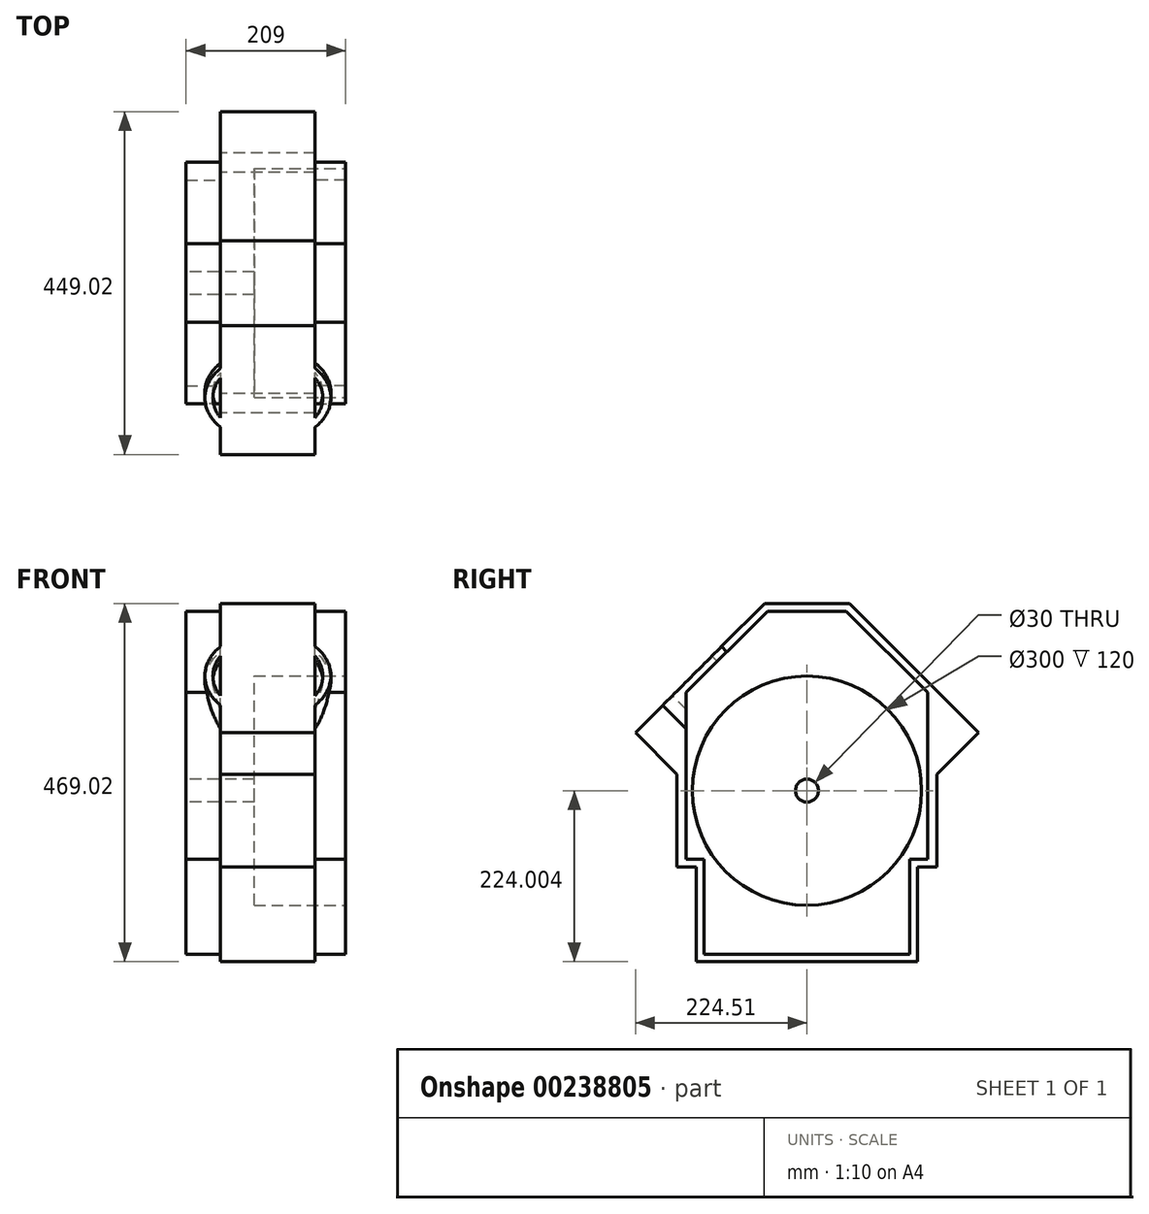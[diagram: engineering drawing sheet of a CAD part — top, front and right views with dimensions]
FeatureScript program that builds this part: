
annotation { "Feature Type Name" : "Feature", "Feature Type Description" : "" }
export const myFeature = defineFeature(function(context is Context, id is Id, definition is map)
    precondition{}
    {
        {
            var Q0;
            Q0=qCreatedBy(makeId("Right.planeOp"),FACE);
            var sketch = newSketch(context, id + "F0", { "sketchPlane" : qUnion([Q0])});
            skLineSegment(sketch, "E0", {"start": v(-150.26, 139.75) * mm, "end": v(-224.5, 65.5) * mm});
            skLineSegment(sketch, "E1", {"start": v(-150.26, 139.75) * mm, "end": v(-55.5, 234.5) * mm});
            skLineSegment(sketch, "E2", {"start": v(-55.5, 234.5) * mm, "end": v(55.5, 234.5) * mm});
            skLineSegment(sketch, "E3", {"start": v(150.26, 139.75) * mm, "end": v(55.5, 234.5) * mm});
            skLineSegment(sketch, "E4", {"start": v(150.26, 139.75) * mm, "end": v(224.5, 65.5) * mm});
            skLineSegment(sketch, "E5", {"start": v(170, 11) * mm, "end": v(224.5, 65.5) * mm});
            skLineSegment(sketch, "E6", {"start": v(170, 11) * mm, "end": v(170, -110.5) * mm});
            skLineSegment(sketch, "E7", {"start": v(144.78, -110.5) * mm, "end": v(170, -110.5) * mm});
            skLineSegment(sketch, "E8", {"start": v(144.78, -110.5) * mm, "end": v(144.78, -234.5) * mm});
            skLineSegment(sketch, "E9", {"start": v(-144.78, -234.5) * mm, "end": v(144.78, -234.5) * mm});
            skLineSegment(sketch, "E10", {"start": v(-144.78, -110.5) * mm, "end": v(-144.78, -234.5) * mm});
            skLineSegment(sketch, "E11", {"start": v(-144.78, -110.5) * mm, "end": v(-170, -110.5) * mm});
            skLineSegment(sketch, "E12", {"start": v(-170, 11) * mm, "end": v(-170, -110.5) * mm});
            skLineSegment(sketch, "E13", {"start": v(-170, 11) * mm, "end": v(-224.5, 65.5) * mm});
            skCircle(sketch, "E14", {"center": v(0, -10.5) * mm, "radius": 15 * mm});
            skSolve(sketch);
        }
        {
            var Q0;
            Q0=makeQuery(id+"F0.imprint","IMPRINT",FACE,{"disambiguationData":[TD([[makeQuery(id+"F0.imprint","IMPRINT",EDGE,{"derivedFrom":sQuery(id+"F0.wireOp",EDGE,"E0")}),1.0]])]});
            extrude(context, id + "F1", {"entities" : qUnion([Q0]), "depth" : 124 * mm});
        }
        {
            var Q0;
            Q0=makeQuery(id+"F1.opExtrude","CAP_FACE",FACE,{"disambiguationData":[OSD([sQuery(id+"F0.wireOp",EDGE,"E0"),sQuery(id+"F0.wireOp",EDGE,"E1"),sQuery(id+"F0.wireOp",EDGE,"E2"),sQuery(id+"F0.wireOp",EDGE,"E3"),sQuery(id+"F0.wireOp",EDGE,"E4"),sQuery(id+"F0.wireOp",EDGE,"E5"),sQuery(id+"F0.wireOp",EDGE,"E6"),sQuery(id+"F0.wireOp",EDGE,"E7"),sQuery(id+"F0.wireOp",EDGE,"E8"),sQuery(id+"F0.wireOp",EDGE,"E9"),sQuery(id+"F0.wireOp",EDGE,"E10"),sQuery(id+"F0.wireOp",EDGE,"E11"),sQuery(id+"F0.wireOp",EDGE,"E12"),sQuery(id+"F0.wireOp",EDGE,"E13"),sQuery(id+"F0.wireOp",EDGE,"E14")])],"isStart":false});
            var sketch = newSketch(context, id + "F2", { "sketchPlane" : qUnion([Q0])});
            skLineSegment(sketch, "E15.bottom", {"start": v(-51.37, 224.5) * mm, "end": v(0, 224.5) * mm});
            skPoint(sketch, "E16", {"position": v(0, -10.5) * mm});
            skLineSegment(sketch, "E17.0", {"start": v(-224.5, 65.5) * mm, "end": v(-55.5, 234.5) * mm});
            skLineSegment(sketch, "E18.0", {"start": v(-158, 117.87) * mm, "end": v(-51.37, 224.5) * mm});
            skLineSegment(sketch, "E19", {"start": v(0, -10.5) * mm, "end": v(0, 224.5) * mm});
            skPoint(sketch, "E20.MirrorCS.start.orphan", {"position": v(90, 185.87) * mm});
            skLineSegment(sketch, "E21", {"start": v(-158, -100.5) * mm, "end": v(-158, 117.87) * mm});
            skPoint(sketch, "E22.orphan", {"position": v(-90, 185.87) * mm});
            skLineSegment(sketch, "E23", {"start": v(-158, -100.5) * mm, "end": v(-134.78, -100.5) * mm});
            skLineSegment(sketch, "E24", {"start": v(-134.78, -100.5) * mm, "end": v(-134.78, -224.5) * mm});
            skLineSegment(sketch, "E25", {"start": v(-134.78, -224.5) * mm, "end": v(0, -224.5) * mm});
            skPoint(sketch, "E26.orphan", {"position": v(51.37, 224.5) * mm});
            skLineSegment(sketch, "E27.MirrorCS", {"start": v(51.37, 224.5) * mm, "end": v(0, 224.5) * mm});
            skLineSegment(sketch, "E28.MirrorCS", {"start": v(158, 117.87) * mm, "end": v(51.37, 224.5) * mm});
            skLineSegment(sketch, "E29.MirrorCS", {"start": v(158, -100.5) * mm, "end": v(158, 117.87) * mm});
            skLineSegment(sketch, "E30.MirrorCS", {"start": v(158, -100.5) * mm, "end": v(134.78, -100.5) * mm});
            skLineSegment(sketch, "E31.MirrorCS", {"start": v(134.78, -100.5) * mm, "end": v(134.78, -224.5) * mm});
            skLineSegment(sketch, "E32.MirrorCS", {"start": v(134.78, -224.5) * mm, "end": v(0, -224.5) * mm});
            skSolve(sketch);
        }
        {
            var Q0;
            Q0=makeQuery(id+"F2.imprint","IMPRINT",FACE,{"disambiguationData":[TD([[makeQuery(id+"F2.imprint","IMPRINT",EDGE,{"derivedFrom":sQuery(id+"F2.wireOp",EDGE,"E15.bottom")}),-1.0]])]});
            extrude(context, id + "F3", {"entities" : qUnion([Q0]), "operationType" : NewBodyOperationType.ADD, "depth" : 40 * mm});
        }
        {
            var Q0;
            Q0=makeQuery(id+"F1.opExtrude","CAP_FACE",FACE,{"disambiguationData":[OSD([sQuery(id+"F0.wireOp",EDGE,"E0"),sQuery(id+"F0.wireOp",EDGE,"E1"),sQuery(id+"F0.wireOp",EDGE,"E2"),sQuery(id+"F0.wireOp",EDGE,"E3"),sQuery(id+"F0.wireOp",EDGE,"E4"),sQuery(id+"F0.wireOp",EDGE,"E5"),sQuery(id+"F0.wireOp",EDGE,"E6"),sQuery(id+"F0.wireOp",EDGE,"E7"),sQuery(id+"F0.wireOp",EDGE,"E8"),sQuery(id+"F0.wireOp",EDGE,"E9"),sQuery(id+"F0.wireOp",EDGE,"E10"),sQuery(id+"F0.wireOp",EDGE,"E11"),sQuery(id+"F0.wireOp",EDGE,"E12"),sQuery(id+"F0.wireOp",EDGE,"E13"),sQuery(id+"F0.wireOp",EDGE,"E14")])],"isStart":true});
            var sketch = newSketch(context, id + "F4", { "sketchPlane" : qUnion([Q0])});
            skLineSegment(sketch, "E33.0", {"start": v(158, -100.5) * mm, "end": v(158, 117.87) * mm});
            skLineSegment(sketch, "E33.1", {"start": v(158, 117.87) * mm, "end": v(51.37, 224.5) * mm});
            skLineSegment(sketch, "E33.2", {"start": v(51.37, 224.5) * mm, "end": v(0, 224.5) * mm});
            skLineSegment(sketch, "E33.3", {"start": v(-51.37, 224.5) * mm, "end": v(0, 224.5) * mm});
            skLineSegment(sketch, "E33.4", {"start": v(-158, 117.87) * mm, "end": v(-51.37, 224.5) * mm});
            skLineSegment(sketch, "E33.5", {"start": v(-158, -100.5) * mm, "end": v(-158, 117.87) * mm});
            skLineSegment(sketch, "E33.6", {"start": v(-134.78, -100.5) * mm, "end": v(-134.78, -224.5) * mm});
            skLineSegment(sketch, "E33.7", {"start": v(-134.78, -224.5) * mm, "end": v(0, -224.5) * mm});
            skLineSegment(sketch, "E33.8", {"start": v(134.78, -224.5) * mm, "end": v(0, -224.5) * mm});
            skLineSegment(sketch, "E33.9", {"start": v(134.78, -100.5) * mm, "end": v(134.78, -224.5) * mm});
            skLineSegment(sketch, "E33.10", {"start": v(158, -100.5) * mm, "end": v(134.78, -100.5) * mm});
            skLineSegment(sketch, "E33.11", {"start": v(-158, -100.5) * mm, "end": v(-134.78, -100.5) * mm});
            skSolve(sketch);
        }
        {
            var Q0;
            Q0=makeQuery(id+"F4.imprint","IMPRINT",FACE,{"disambiguationData":[TD([[makeQuery(id+"F4.imprint","IMPRINT",EDGE,{"derivedFrom":sQuery(id+"F4.wireOp",EDGE,"E33.0")}),1.0]])]});
            extrude(context, id + "F5", {"entities" : qUnion([Q0]), "operationType" : NewBodyOperationType.ADD, "depth" : 45 * mm});
        }
        {
            var Q0;
            Q0=makeQuery(id+"F1.opExtrude","SWEPT_FACE",FACE,{"disambiguationData":[OSD([sQuery(id+"F0.wireOp",EDGE,"E0"),sQuery(id+"F0.wireOp",EDGE,"E1")])]});
            var sketch = newSketch(context, id + "F6", { "sketchPlane" : qUnion([Q0])});
            skCircle(sketch, "E34", {"center": v(62, -7.43) * mm, "radius": 82.5 * mm});
            skPoint(sketch, "E34.centerSnap0", {"position": v(62, -112.43) * mm});
            skCircle(sketch, "E35", {"center": v(62, -7.43) * mm, "radius": 72 * mm});
            skSolve(sketch);
        }
        {
            var Q0;
            {var subQ0=sQuery(id+"F6.wireOp",EDGE,"E34");var subQ1=makeQuery(id+"F1.opExtrude","CAP_EDGE",EDGE,{"disambiguationData":[OSD([sQuery(id+"F0.wireOp",EDGE,"E0"),sQuery(id+"F0.wireOp",EDGE,"E1")])],"isStart":false});var subQ2=makeQuery(id+"F6.imprint","INTERSECT",VERTEX,{"disambiguationData":[OD(0.0)],"derivedFrom":[subQ1,subQ0]});Q0=makeQuery(id+"F6.imprint","IMPRINT",FACE,{"disambiguationData":[TD([[makeQuery(id+"F6.imprint","IMPRINT",EDGE,{"disambiguationData":[TD([[subQ2,1.0]])],"derivedFrom":subQ0}),1.0]])]});}
            var Q1;
            {var subQ0=sQuery(id+"F6.wireOp",EDGE,"E34");var subQ1=makeQuery(id+"F1.opExtrude","CAP_EDGE",EDGE,{"disambiguationData":[OSD([sQuery(id+"F0.wireOp",EDGE,"E0"),sQuery(id+"F0.wireOp",EDGE,"E1")])],"isStart":true});var subQ2=makeQuery(id+"F6.imprint","INTERSECT",VERTEX,{"disambiguationData":[OD(0.0)],"derivedFrom":[subQ1,subQ0]});Q1=makeQuery(id+"F6.imprint","IMPRINT",FACE,{"disambiguationData":[TD([[makeQuery(id+"F6.imprint","IMPRINT",EDGE,{"disambiguationData":[TD([[subQ2,-1.0]])],"derivedFrom":subQ0}),1.0]])]});}
            extrude(context, id + "F7", {"entities" : qUnion([Q0, Q1]), "operationType" : NewBodyOperationType.ADD, "oppositeDirection" : true, "depth" : 100 * mm});
        }
        {
            var Q0;
            Q0=makeQuery(id+"F3.opExtrude","CAP_FACE",FACE,{"disambiguationData":[OSD([sQuery(id+"F0.wireOp",EDGE,"E14"),sQuery(id+"F2.wireOp",EDGE,"E15.bottom"),sQuery(id+"F2.wireOp",EDGE,"E18.0"),sQuery(id+"F2.wireOp",EDGE,"E21"),sQuery(id+"F2.wireOp",EDGE,"E23"),sQuery(id+"F2.wireOp",EDGE,"E24"),sQuery(id+"F2.wireOp",EDGE,"E25"),sQuery(id+"F2.wireOp",EDGE,"E27.MirrorCS"),sQuery(id+"F2.wireOp",EDGE,"E28.MirrorCS"),sQuery(id+"F2.wireOp",EDGE,"E29.MirrorCS"),sQuery(id+"F2.wireOp",EDGE,"E30.MirrorCS"),sQuery(id+"F2.wireOp",EDGE,"E31.MirrorCS"),sQuery(id+"F2.wireOp",EDGE,"E32.MirrorCS")])],"isStart":false});
            var sketch = newSketch(context, id + "F8", { "sketchPlane" : qUnion([Q0])});
            skCircle(sketch, "E36", {"center": v(0, -10.5) * mm, "radius": 150 * mm});
            skSolve(sketch);
        }
        {
            var Q0;
            Q0=makeQuery(id+"F8.imprint","IMPRINT",FACE,{"disambiguationData":[TD([[makeQuery(id+"F8.imprint","IMPRINT",EDGE,{"derivedFrom":sQuery(id+"F8.wireOp",EDGE,"E36")}),1.0]])]});
            extrude(context, id + "F9", {"entities" : qUnion([Q0]), "operationType" : NewBodyOperationType.REMOVE, "oppositeDirection" : true, "depth" : 120 * mm});
        }
    });
